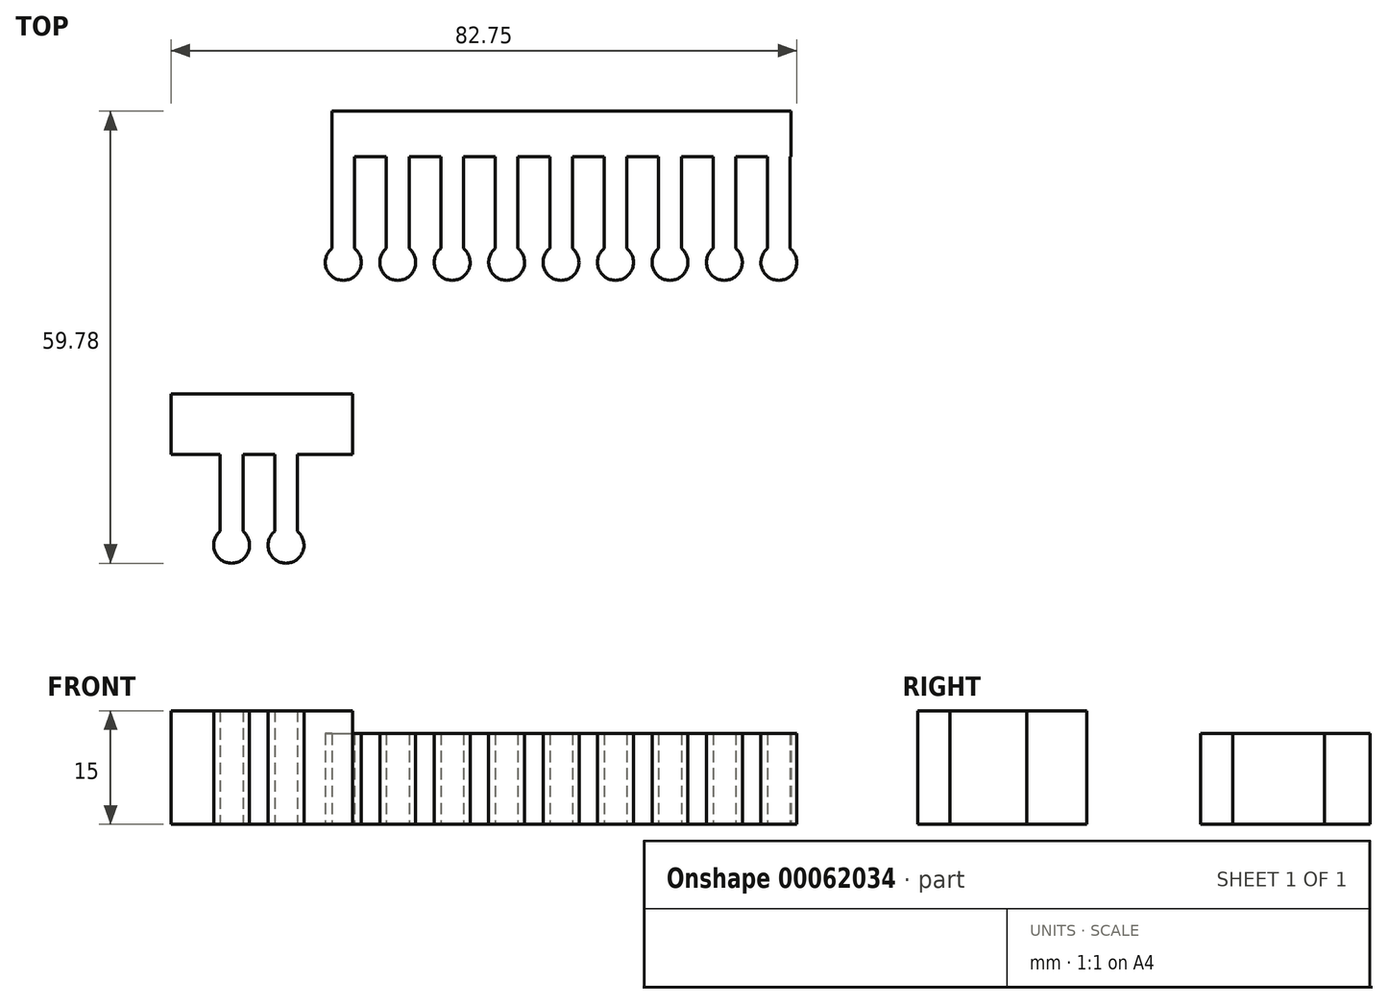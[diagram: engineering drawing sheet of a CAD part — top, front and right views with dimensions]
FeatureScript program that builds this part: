
annotation { "Feature Type Name" : "Feature", "Feature Type Description" : "" }
export const myFeature = defineFeature(function(context is Context, id is Id, definition is map)
    precondition{}
    {
        {
            var Q0;
            Q0=qCreatedBy(makeId("Top.planeOp"),FACE);
            var sketch = newSketch(context, id + "F0", { "sketchPlane" : qUnion([Q0])});
            skLineSegment(sketch, "E0.bottom", {"start": v(-61.48, 48.48) * mm, "end": v(-0.78, 48.48) * mm});
            skLineSegment(sketch, "E0.top", {"start": v(-61.48, 42.48) * mm, "end": v(-0.78, 42.48) * mm});
            skLineSegment(sketch, "E0.left", {"start": v(-61.48, 48.48) * mm, "end": v(-61.48, 42.48) * mm});
            skLineSegment(sketch, "E0.right", {"start": v(-0.78, 48.48) * mm, "end": v(-0.78, 42.48) * mm});
            skLineSegment(sketch, "E1.bottom", {"start": v(-61.48, 48.48) * mm, "end": v(-58.48, 48.48) * mm});
            skLineSegment(sketch, "E1.top", {"start": v(-61.48, 28.48) * mm, "end": v(-58.48, 28.48) * mm});
            skLineSegment(sketch, "E1.left", {"start": v(-61.48, 48.48) * mm, "end": v(-61.48, 28.48) * mm});
            skLineSegment(sketch, "E1.right", {"start": v(-58.48, 48.48) * mm, "end": v(-58.48, 28.48) * mm});
            skLineSegment(sketch, "E2.bottom", {"start": v(-54.28, 48.48) * mm, "end": v(-51.28, 48.48) * mm});
            skLineSegment(sketch, "E2.top", {"start": v(-54.28, 28.48) * mm, "end": v(-51.28, 28.48) * mm});
            skLineSegment(sketch, "E2.left", {"start": v(-54.28, 48.48) * mm, "end": v(-54.28, 28.48) * mm});
            skLineSegment(sketch, "E2.right", {"start": v(-51.28, 48.48) * mm, "end": v(-51.28, 28.48) * mm});
            skLineSegment(sketch, "E3.bottom", {"start": v(-47.08, 48.48) * mm, "end": v(-44.08, 48.48) * mm});
            skLineSegment(sketch, "E3.top", {"start": v(-47.08, 28.48) * mm, "end": v(-44.08, 28.48) * mm});
            skLineSegment(sketch, "E3.left", {"start": v(-47.08, 48.48) * mm, "end": v(-47.08, 28.48) * mm});
            skLineSegment(sketch, "E3.right", {"start": v(-44.08, 48.48) * mm, "end": v(-44.08, 28.48) * mm});
            skLineSegment(sketch, "E4.bottom", {"start": v(-39.88, 48.48) * mm, "end": v(-36.88, 48.48) * mm});
            skLineSegment(sketch, "E4.top", {"start": v(-39.88, 28.48) * mm, "end": v(-36.88, 28.48) * mm});
            skLineSegment(sketch, "E4.left", {"start": v(-39.88, 48.48) * mm, "end": v(-39.88, 28.48) * mm});
            skLineSegment(sketch, "E4.right", {"start": v(-36.88, 48.48) * mm, "end": v(-36.88, 28.48) * mm});
            skLineSegment(sketch, "E5.bottom", {"start": v(-32.68, 48.48) * mm, "end": v(-29.68, 48.48) * mm});
            skLineSegment(sketch, "E5.top", {"start": v(-32.68, 28.48) * mm, "end": v(-29.68, 28.48) * mm});
            skLineSegment(sketch, "E5.left", {"start": v(-32.68, 48.48) * mm, "end": v(-32.68, 28.48) * mm});
            skLineSegment(sketch, "E5.right", {"start": v(-29.68, 48.48) * mm, "end": v(-29.68, 28.48) * mm});
            skLineSegment(sketch, "E6.bottom", {"start": v(-25.48, 48.48) * mm, "end": v(-22.48, 48.48) * mm});
            skLineSegment(sketch, "E6.top", {"start": v(-25.48, 28.48) * mm, "end": v(-22.48, 28.48) * mm});
            skLineSegment(sketch, "E6.left", {"start": v(-25.48, 48.48) * mm, "end": v(-25.48, 28.48) * mm});
            skLineSegment(sketch, "E6.right", {"start": v(-22.48, 48.48) * mm, "end": v(-22.48, 28.48) * mm});
            skLineSegment(sketch, "E7.bottom", {"start": v(-18.28, 48.48) * mm, "end": v(-15.28, 48.48) * mm});
            skLineSegment(sketch, "E7.top", {"start": v(-18.28, 28.48) * mm, "end": v(-15.28, 28.48) * mm});
            skLineSegment(sketch, "E7.left", {"start": v(-18.28, 48.48) * mm, "end": v(-18.28, 28.48) * mm});
            skLineSegment(sketch, "E7.right", {"start": v(-15.28, 48.48) * mm, "end": v(-15.28, 28.48) * mm});
            skLineSegment(sketch, "E8.bottom", {"start": v(-11.08, 48.48) * mm, "end": v(-8.08, 48.48) * mm});
            skLineSegment(sketch, "E8.top", {"start": v(-11.08, 28.48) * mm, "end": v(-8.08, 28.48) * mm});
            skLineSegment(sketch, "E8.left", {"start": v(-11.08, 48.48) * mm, "end": v(-11.08, 28.48) * mm});
            skLineSegment(sketch, "E8.right", {"start": v(-8.08, 48.48) * mm, "end": v(-8.08, 28.48) * mm});
            skLineSegment(sketch, "E9.bottom", {"start": v(-3.88, 48.48) * mm, "end": v(-0.88, 48.48) * mm});
            skLineSegment(sketch, "E9.top", {"start": v(-3.88, 28.48) * mm, "end": v(-0.88, 28.48) * mm});
            skLineSegment(sketch, "E9.left", {"start": v(-3.88, 48.48) * mm, "end": v(-3.88, 28.48) * mm});
            skLineSegment(sketch, "E9.right", {"start": v(-0.88, 48.48) * mm, "end": v(-0.88, 28.48) * mm});
            skCircle(sketch, "E10", {"center": v(-59.98, 28.48) * mm, "radius": 2.38 * mm});
            skCircle(sketch, "E11", {"center": v(-52.78, 28.48) * mm, "radius": 2.38 * mm});
            skCircle(sketch, "E12", {"center": v(-45.58, 28.48) * mm, "radius": 2.38 * mm});
            skCircle(sketch, "E13", {"center": v(-38.38, 28.48) * mm, "radius": 2.38 * mm});
            skCircle(sketch, "E14", {"center": v(-31.18, 28.48) * mm, "radius": 2.38 * mm});
            skCircle(sketch, "E15", {"center": v(-16.78, 28.48) * mm, "radius": 2.38 * mm});
            skCircle(sketch, "E16", {"center": v(-23.98, 28.48) * mm, "radius": 2.38 * mm});
            skCircle(sketch, "E17", {"center": v(-9.58, 28.48) * mm, "radius": 2.38 * mm});
            skCircle(sketch, "E18", {"center": v(-2.38, 28.48) * mm, "radius": 2.38 * mm});
            skSolve(sketch);
        }
        {
            var Q0;
            Q0 = qSketchRegion(id + "F0", true);
            extrude(context, id + "F1", {"entities" : qUnion([Q0]), "depth" : 12 * mm});
        }
        {
            var Q0;
            Q0=qCreatedBy(makeId("Top.planeOp"),FACE);
            var sketch = newSketch(context, id + "F2", { "sketchPlane" : qUnion([Q0])});
            skLineSegment(sketch, "E19.bottom", {"start": v(-76.25, 9.08) * mm, "end": v(-65.25, 9.08) * mm});
            skLineSegment(sketch, "E19.top", {"start": v(-76.25, 3.08) * mm, "end": v(-65.25, 3.08) * mm});
            skLineSegment(sketch, "E19.left", {"start": v(-76.25, 9.08) * mm, "end": v(-76.25, 3.08) * mm});
            skLineSegment(sketch, "E19.right", {"start": v(-65.25, 9.08) * mm, "end": v(-65.25, 3.08) * mm});
            skLineSegment(sketch, "E20.bottom", {"start": v(-76.25, 9.08) * mm, "end": v(-73.25, 9.08) * mm});
            skLineSegment(sketch, "E20.top", {"start": v(-76.25, -8.92) * mm, "end": v(-73.25, -8.92) * mm});
            skLineSegment(sketch, "E20.left", {"start": v(-76.25, 9.08) * mm, "end": v(-76.25, -8.92) * mm});
            skLineSegment(sketch, "E20.right", {"start": v(-73.25, 9.08) * mm, "end": v(-73.25, -8.92) * mm});
            skLineSegment(sketch, "E21.bottom", {"start": v(-69.05, 9.08) * mm, "end": v(-66.05, 9.08) * mm});
            skLineSegment(sketch, "E21.top", {"start": v(-69.05, -8.92) * mm, "end": v(-66.05, -8.92) * mm});
            skLineSegment(sketch, "E21.left", {"start": v(-69.05, 9.08) * mm, "end": v(-69.05, -8.92) * mm});
            skLineSegment(sketch, "E21.right", {"start": v(-66.05, 9.08) * mm, "end": v(-66.05, -8.92) * mm});
            skCircle(sketch, "E22", {"center": v(-74.75, -8.92) * mm, "radius": 2.38 * mm});
            skCircle(sketch, "E23", {"center": v(-67.55, -8.92) * mm, "radius": 2.38 * mm});
            skLineSegment(sketch, "E24.bottom", {"start": v(-70.75, 3.08) * mm, "end": v(-82.75, 3.08) * mm});
            skLineSegment(sketch, "E24.top", {"start": v(-70.75, 11.08) * mm, "end": v(-82.75, 11.08) * mm});
            skLineSegment(sketch, "E24.left", {"start": v(-70.75, 3.08) * mm, "end": v(-70.75, 11.08) * mm});
            skLineSegment(sketch, "E24.right", {"start": v(-82.75, 3.08) * mm, "end": v(-82.75, 11.08) * mm});
            skLineSegment(sketch, "E25.bottom", {"start": v(-70.75, 3.08) * mm, "end": v(-58.75, 3.08) * mm});
            skLineSegment(sketch, "E25.top", {"start": v(-70.75, 11.08) * mm, "end": v(-58.75, 11.08) * mm});
            skLineSegment(sketch, "E25.right", {"start": v(-58.75, 3.08) * mm, "end": v(-58.75, 11.08) * mm});
            skSolve(sketch);
        }
        {
            var Q0;
            Q0 = qSketchRegion(id + "F2", true);
            extrude(context, id + "F3", {"entities" : qUnion([Q0]), "depth" : 15 * mm});
        }
    });
